# Revit family: 94-ONE PIECE NEW MONZA
name_source: partatom
category: Aparatos sanitarios
units: mm (PartAtom-declared; Revit-internal decimal feet)

## family parameters
Anfitrión = Muro
Compartido = Sí
Corte con vacíos al cargar = Sí
Cota de conector redondo = Diámetro de uso
Número OmniClass = 23.45.00.00
Punto de cálculo de habitación = No
Siempre vertical = Sí
Tipo de pieza = Normal
Título OmniClass = Sanitary, Laundry, and Cleaning Equipment

## types (1)
- ONE PIECE NEW MONZA
    Elevación por defecto = 0 cm
    F_Alto = 60.8 cm
    F_Ancho = 39.1 cm
    F_Certificación = Producto certificado por CESMEC en base al cumplimiento de la Norma Chilena NCh 407 2012 para Artefactos Sanitarios de loza vítrea, según modelo de certificación ISO CASCO 1
    F_Color = Blanco
    F_Consumo / Capacidad de agua (L) = 4.1 / 6 L
    F_Descripción = Inodorode una pieza con descarga dual de 4,1/6 L,con sistema jet para mejor evacuación. Con asiento cierre suave
    F_Distancia de instalación a muro terminado = 30.5 cm
    F_Peso = 36 kgf
    F_Productos incluidos = Asiento, fitting, sello de cera
    F_Productos necesarios para instalación = Flexible 1/2" x 15/16" Hi-HI 30 cm, Llave Angular 1/2"x 1/2" HE-HE
    F_Profundidad = 75 cm
    F_SKU = CS0071191301CF
    F_Tipo de aro = Elongado
    F_Tipo de instalación = A piso
    F_Tolerancia dimensional = <20 cm:+- 3%, >20 cm: 0,6 cm máx.
    URL = https://www.fanaloza.cl

## geometry (parser evidence)
native form markers: Sweep x1
no freeform markers — native parametric forms only
